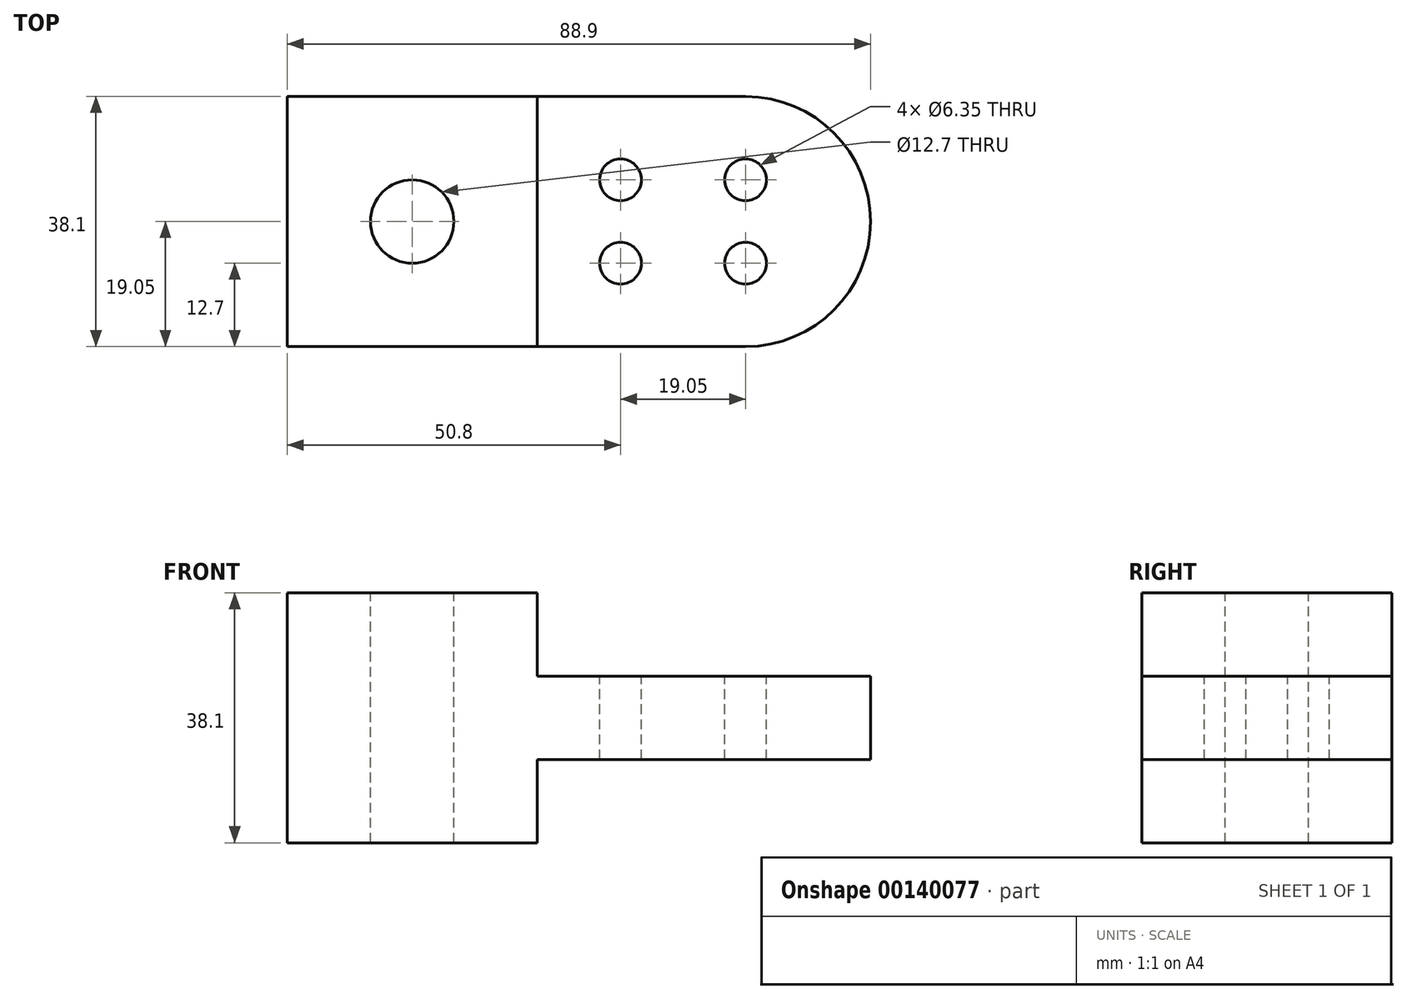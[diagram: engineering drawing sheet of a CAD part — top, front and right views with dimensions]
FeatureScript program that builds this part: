
annotation { "Feature Type Name" : "Feature", "Feature Type Description" : "" }
export const myFeature = defineFeature(function(context is Context, id is Id, definition is map)
    precondition{}
    {
        {
            var Q0;
            Q0=qCreatedBy(makeId("Front.planeOp"),FACE);
            var sketch = newSketch(context, id + "F0", { "sketchPlane" : qUnion([Q0])});
            skLineSegment(sketch, "E0", {"start": v(0, 0) * mm, "end": v(0, 12.7) * mm});
            skLineSegment(sketch, "E1", {"start": v(0, 12.7) * mm, "end": v(50.8, 12.7) * mm});
            skLineSegment(sketch, "E2", {"start": v(50.8, 12.7) * mm, "end": v(50.8, 25.4) * mm});
            skLineSegment(sketch, "E3", {"start": v(50.8, 25.4) * mm, "end": v(0, 25.4) * mm});
            skLineSegment(sketch, "E4", {"start": v(0, 25.4) * mm, "end": v(0, 38.1) * mm});
            skLineSegment(sketch, "E5", {"start": v(0, 38.1) * mm, "end": v(-38.1, 38.1) * mm});
            skLineSegment(sketch, "E6", {"start": v(-38.1, 38.1) * mm, "end": v(-38.1, 0) * mm});
            skLineSegment(sketch, "E7", {"start": v(-38.1, 0) * mm, "end": v(0, 0) * mm});
            skSolve(sketch);
        }
        {
            var Q0;
            Q0=makeQuery(id+"F0.imprint","IMPRINT",FACE,{"disambiguationData":[TD([[makeQuery(id+"F0.imprint","IMPRINT",EDGE,{"derivedFrom":sQuery(id+"F0.wireOp",EDGE,"E0")}),1.0]])]});
            extrude(context, id + "F1", {"entities" : qUnion([Q0]), "depth" : 38.1 * mm});
        }
        {
            var Q0;
            Q0=makeQuery(id+"F1.opExtrude","CAP_EDGE",EDGE,{"disambiguationData":[OSD([sQuery(id+"F0.wireOp",EDGE,"E2")])],"isStart":false});
            var Q1;
            Q1=makeQuery(id+"F1.opExtrude","CAP_EDGE",EDGE,{"disambiguationData":[OSD([sQuery(id+"F0.wireOp",EDGE,"E2")])],"isStart":true});
            fillet(context, id + "F2", {"entities" : qUnion([Q0, Q1]), "radius" : 19.05 * mm, "tangentPropagation" : true, "allowEdgeOverflow" : false});
        }
        {
            var Q0;
            Q0=makeQuery(id+"F1.opExtrude","SWEPT_FACE",FACE,{"disambiguationData":[OSD([sQuery(id+"F0.wireOp",EDGE,"E5")])]});
            var sketch = newSketch(context, id + "F3", { "sketchPlane" : qUnion([Q0])});
            skLineSegment(sketch, "E8", {"start": v(-41.4, -19.05) * mm, "end": v(92.55, -19.05) * mm, "construction": true});
            skLineSegment(sketch, "E9", {"start": v(0, -12.7) * mm, "end": v(60.43, -12.7) * mm, "construction": true});
            skLineSegment(sketch, "E10", {"start": v(0, -25.4) * mm, "end": v(55.92, -25.4) * mm, "construction": true});
            skCircle(sketch, "E11", {"center": v(-19.05, -19.05) * mm, "radius": 6.35 * mm});
            skCircle(sketch, "E12", {"center": v(12.7, -12.7) * mm, "radius": 3.18 * mm});
            skCircle(sketch, "E13", {"center": v(31.75, -12.7) * mm, "radius": 3.18 * mm});
            skCircle(sketch, "E14", {"center": v(12.7, -25.4) * mm, "radius": 3.18 * mm});
            skCircle(sketch, "E15", {"center": v(31.75, -25.4) * mm, "radius": 3.18 * mm});
            skPoint(sketch, "E16", {"position": v(30.22, -12.7) * mm});
            skSolve(sketch);
        }
        {
            var Q0;
            Q0 = qSketchRegion(id + "F3", true);
            extrude(context, id + "F4", {"entities" : qUnion([Q0]), "operationType" : NewBodyOperationType.REMOVE, "endBound" : BoundingType.THROUGH_ALL, "oppositeDirection" : true, "depth" : 25.4 * mm});
        }
    });
